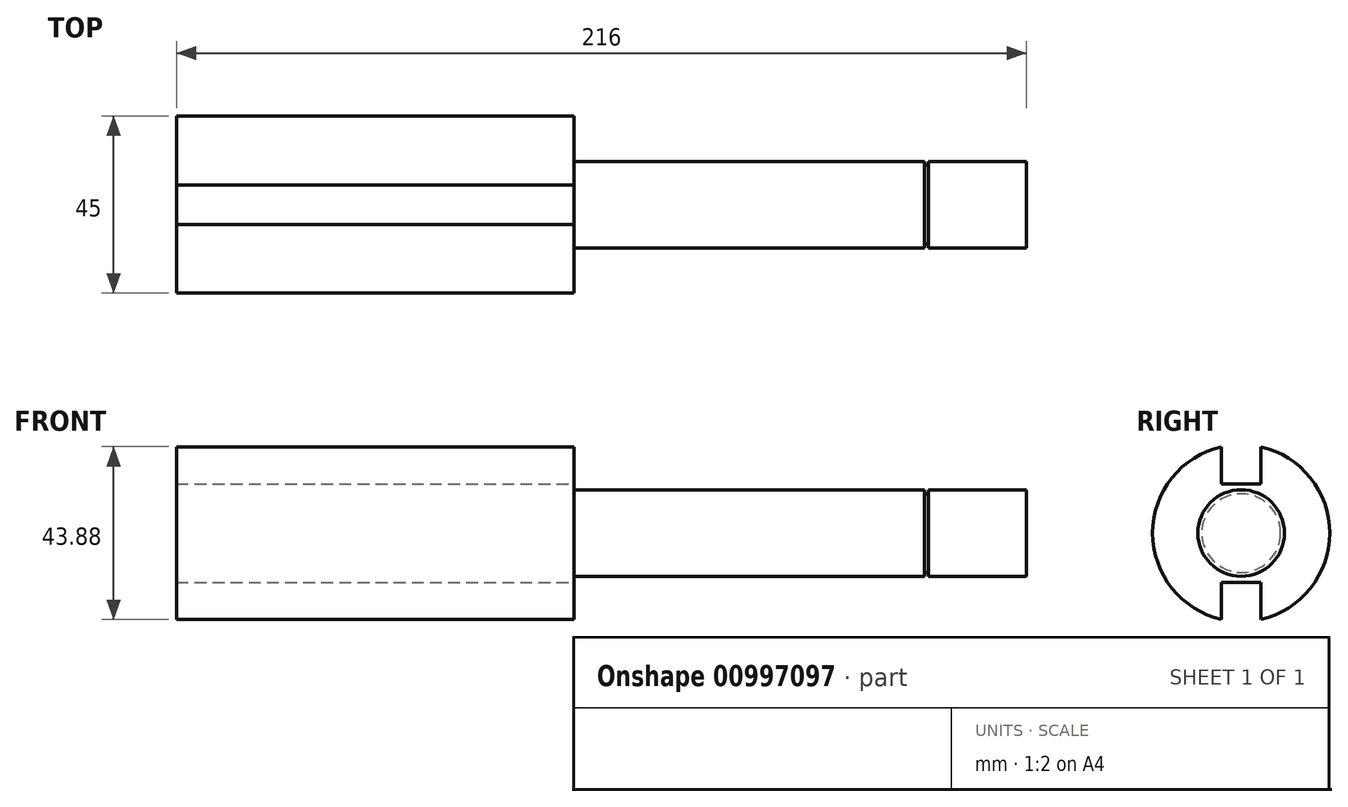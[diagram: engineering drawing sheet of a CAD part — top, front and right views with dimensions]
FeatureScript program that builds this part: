
annotation { "Feature Type Name" : "Feature", "Feature Type Description" : "" }
export const myFeature = defineFeature(function(context is Context, id is Id, definition is map)
    precondition{}
    {
        {
            var Q0;
            Q0=qCreatedBy(makeId("Front.planeOp"),FACE);
            var sketch = newSketch(context, id + "F0", { "sketchPlane" : qUnion([Q0])});
            skLineSegment(sketch, "E0", {"start": v(0, 0) * mm, "end": v(0, 22.5) * mm});
            skLineSegment(sketch, "E1", {"start": v(0, 22.5) * mm, "end": v(101, 22.5) * mm});
            skLineSegment(sketch, "E2", {"start": v(101, 22.5) * mm, "end": v(101, 11) * mm});
            skLineSegment(sketch, "E3", {"start": v(101, 11) * mm, "end": v(190, 11) * mm});
            skLineSegment(sketch, "E4", {"start": v(216, 11) * mm, "end": v(216, 0) * mm});
            skLineSegment(sketch, "E5", {"start": v(216, 0) * mm, "end": v(0, 0) * mm});
            skLineSegment(sketch, "E6", {"start": v(-75.94, 0) * mm, "end": v(247.94, 0) * mm, "construction": true});
            skLineSegment(sketch, "E7.top", {"start": v(190, 10) * mm, "end": v(191, 10) * mm});
            skLineSegment(sketch, "E7.left", {"start": v(190, 11) * mm, "end": v(190, 10) * mm});
            skLineSegment(sketch, "E7.right", {"start": v(191, 11) * mm, "end": v(191, 10) * mm});
            skLineSegment(sketch, "E8.trimOffspring", {"start": v(191, 11) * mm, "end": v(216, 11) * mm});
            skSolve(sketch);
        }
        {
            var Q0;
            Q0 = qSketchRegion(id + "F0", true);
            var Q1;
            Q1=sQuery(id+"F0.wireOp",EDGE,"E6");
            revolve(context, id + "F1", {"surfaceOperationType" : NewSurfaceOperationType.NEW, "entities" : qUnion([Q0]), "axis" : qUnion([Q1]), "revolveType" : RevolveType.FULL});
        }
        {
            var Q0;
            Q0=makeQuery(id+"F1.opRevolve","SWEPT_FACE",FACE,{"disambiguationData":[OSD([sQuery(id+"F0.wireOp",EDGE,"E2")])]});
            var sketch = newSketch(context, id + "F2", { "sketchPlane" : qUnion([Q0])});
            skLineSegment(sketch, "E9", {"start": v(-5, 21.94) * mm, "end": v(-5, 12.5) * mm});
            skLineSegment(sketch, "E10", {"start": v(-5, 12.5) * mm, "end": v(5, 12.5) * mm});
            skLineSegment(sketch, "E11", {"start": v(5, 12.5) * mm, "end": v(5, 21.94) * mm});
            skPoint(sketch, "E12", {"position": v(0, 12.5) * mm});
            skArc(sketch, "E13", {"start": v(5, 21.94) * mm, "mid": v(0, 22.5) * mm, "end": v(-5, 21.94) * mm});
            skLineSegment(sketch, "E14.MirrorCS", {"start": v(-5, -21.94) * mm, "end": v(-5, -12.5) * mm});
            skArc(sketch, "E15.MirrorCS", {"start": v(5, -21.94) * mm, "mid": v(0, -22.5) * mm, "end": v(-5, -21.94) * mm});
            skLineSegment(sketch, "E16.MirrorCS", {"start": v(5, -12.5) * mm, "end": v(5, -21.94) * mm});
            skLineSegment(sketch, "E17.MirrorCS", {"start": v(-5, -12.5) * mm, "end": v(5, -12.5) * mm});
            skSolve(sketch);
        }
        {
            var Q0;
            Q0 = qSketchRegion(id + "F2", true);
            extrude(context, id + "F3", {"entities" : qUnion([Q0]), "operationType" : NewBodyOperationType.REMOVE, "oppositeDirection" : true, "depth" : 125 * mm, "offsetDistance" : 25 * mm});
        }
    });
